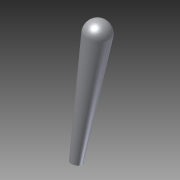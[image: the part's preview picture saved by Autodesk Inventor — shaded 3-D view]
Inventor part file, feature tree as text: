
AUTODESK INVENTOR PART (.ipt)
format: ipt  version: 2011 SP1 (Build 150282100, 282)  size: 89,600 bytes
history: native  units: in
note: dims shown in document units (in); Inventor stores cm internally (conversion verified against a paired STEP export)
features: other x7, revolve x1, sketch x1
ambient origin geometry x8: Origin, YZ Plane, XZ Plane, XY Plane, X Axis, Y Axis, Z Axis, Center Point
bodies: Solid1 (feature_tree)
feature tree (9):
  revolve  "Revolution1"  [1 undecoded]
  other  "toggle_XY"
  other  "toggle_YZ"
  other  "toggle_ZX"
  other  "toggle_X"
  other  "toggle_Y"
  other  "toggle_Z"
  other  "toggle_Center"
  sketch  "Sketch_1"  dims[d0=360.0deg]
note: 1 required parameter value undecoded (feature->parameter linkage not recoverable at this tier; creation-order binding heuristic only, values carry confidence <= 0.55)
